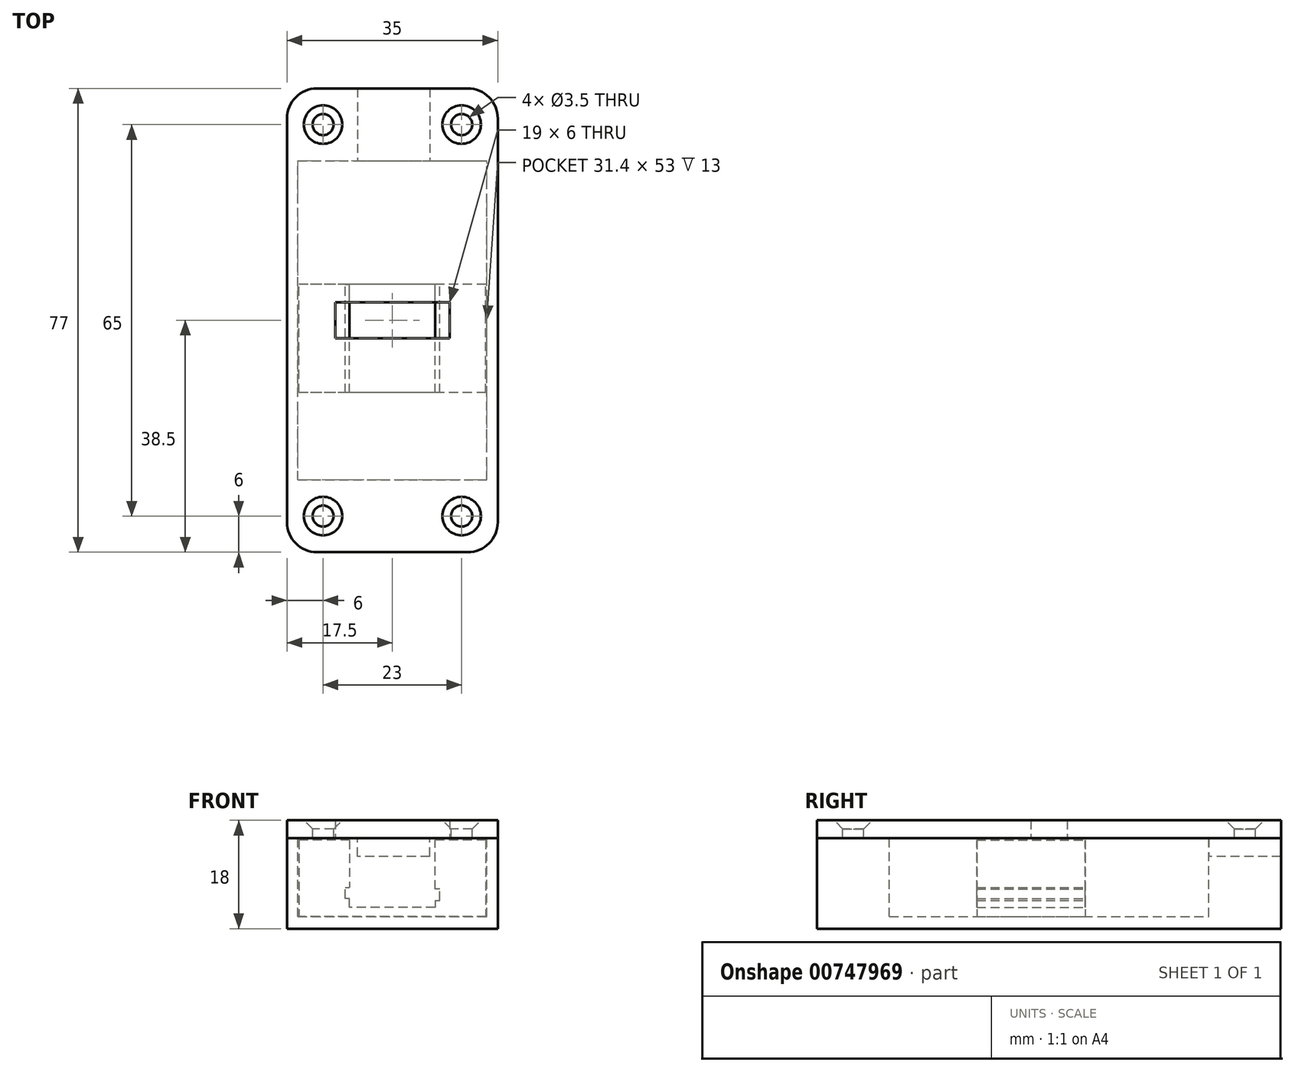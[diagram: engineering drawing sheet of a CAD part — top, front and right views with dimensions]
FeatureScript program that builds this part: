
annotation { "Feature Type Name" : "Feature", "Feature Type Description" : "" }
export const myFeature = defineFeature(function(context is Context, id is Id, definition is map)
    precondition{}
    {
        {
            var Q0;
            Q0=qCreatedBy(makeId("Top.planeOp"),FACE);
            var sketch = newSketch(context, id + "F0", { "sketchPlane" : qUnion([Q0])});
            skLineSegment(sketch, "E0.bottom", {"start": v(0, 0) * mm, "end": v(35, 0) * mm});
            skLineSegment(sketch, "E0.top", {"start": v(0, 77) * mm, "end": v(35, 77) * mm});
            skLineSegment(sketch, "E0.left", {"start": v(0, 0) * mm, "end": v(0, 77) * mm});
            skLineSegment(sketch, "E0.right", {"start": v(35, 0) * mm, "end": v(35, 77) * mm});
            skSolve(sketch);
        }
        {
            var Q0;
            Q0=makeQuery(id+"F0.imprint","IMPRINT",FACE,{"disambiguationData":[TD([[makeQuery(id+"F0.imprint","IMPRINT",EDGE,{"derivedFrom":sQuery(id+"F0.wireOp",EDGE,"E0.bottom")}),1.0]])]});
            extrude(context, id + "F1", {"entities" : qUnion([Q0]), "depth" : 15 * mm, "offsetDistance" : 25 * mm});
        }
        {
            var Q0;
            Q0=makeQuery(id+"F1.opExtrude","CAP_FACE",FACE,{"disambiguationData":[OSD([sQuery(id+"F0.wireOp",EDGE,"E0.bottom"),sQuery(id+"F0.wireOp",EDGE,"E0.top"),sQuery(id+"F0.wireOp",EDGE,"E0.left"),sQuery(id+"F0.wireOp",EDGE,"E0.right")])],"isStart":false});
            var sketch = newSketch(context, id + "F2", { "sketchPlane" : qUnion([Q0])});
            skLineSegment(sketch, "E1.bottom", {"start": v(1.8, 12) * mm, "end": v(33.2, 12) * mm});
            skLineSegment(sketch, "E1.top", {"start": v(1.8, 65) * mm, "end": v(33.2, 65) * mm});
            skLineSegment(sketch, "E1.left", {"start": v(1.8, 12) * mm, "end": v(1.8, 65) * mm});
            skLineSegment(sketch, "E1.right", {"start": v(33.2, 12) * mm, "end": v(33.2, 65) * mm});
            skSolve(sketch);
        }
        {
            var Q0;
            Q0=makeQuery(id+"F2.imprint","IMPRINT",FACE,{"disambiguationData":[TD([[makeQuery(id+"F2.imprint","IMPRINT",EDGE,{"derivedFrom":sQuery(id+"F2.wireOp",EDGE,"E1.bottom")}),1.0]])]});
            extrude(context, id + "F3", {"entities" : qUnion([Q0]), "operationType" : NewBodyOperationType.REMOVE, "oppositeDirection" : true, "depth" : 13 * mm, "offsetDistance" : 25 * mm});
        }
        {
            var Q0;
            Q0=makeQuery(id+"F3.boolean.opBoolean","COPY",FACE,{"derivedFrom":makeQuery(id+"F3.opExtrude","SWEPT_FACE",FACE,{"disambiguationData":[OSD([sQuery(id+"F2.wireOp",EDGE,"E1.top")])]})});
            var sketch = newSketch(context, id + "F4", { "sketchPlane" : qUnion([Q0])});
            skLineSegment(sketch, "E2.bottom", {"start": v(11.7, 15) * mm, "end": v(23.7, 15) * mm});
            skLineSegment(sketch, "E2.top", {"start": v(11.7, 12) * mm, "end": v(23.7, 12) * mm});
            skLineSegment(sketch, "E2.left", {"start": v(11.7, 15) * mm, "end": v(11.7, 12) * mm});
            skLineSegment(sketch, "E2.right", {"start": v(23.7, 15) * mm, "end": v(23.7, 12) * mm});
            skSolve(sketch);
        }
        {
            var Q0;
            Q0=makeQuery(id+"F4.imprint","IMPRINT",FACE,{"disambiguationData":[TD([[makeQuery(id+"F4.imprint","IMPRINT",EDGE,{"derivedFrom":sQuery(id+"F4.wireOp",EDGE,"E2.bottom")}),-1.0]])]});
            extrude(context, id + "F5", {"entities" : qUnion([Q0]), "operationType" : NewBodyOperationType.REMOVE, "oppositeDirection" : true, "depth" : 25 * mm, "offsetDistance" : 25 * mm});
        }
        {
            var Q0;
            Q0=makeQuery(id+"F1.opExtrude","CAP_FACE",FACE,{"disambiguationData":[OSD([sQuery(id+"F0.wireOp",EDGE,"E0.bottom"),sQuery(id+"F0.wireOp",EDGE,"E0.top"),sQuery(id+"F0.wireOp",EDGE,"E0.left"),sQuery(id+"F0.wireOp",EDGE,"E0.right")])],"isStart":false});
            var sketch = newSketch(context, id + "F6", { "sketchPlane" : qUnion([Q0])});
            skCircle(sketch, "E3", {"center": v(6, 6) * mm, "radius": 1.65 * mm});
            skCircle(sketch, "E4", {"center": v(29, 6) * mm, "radius": 1.65 * mm});
            skCircle(sketch, "E5", {"center": v(6, 71) * mm, "radius": 1.65 * mm});
            skCircle(sketch, "E6", {"center": v(29, 71) * mm, "radius": 1.65 * mm});
            skSolve(sketch);
        }
        {
            var Q0;
            Q0=makeQuery(id+"F6.imprint","IMPRINT",FACE,{"disambiguationData":[TD([[makeQuery(id+"F6.imprint","IMPRINT",EDGE,{"derivedFrom":sQuery(id+"F6.wireOp",EDGE,"E3")}),-1.0]])]});
            var sketch = newSketch(context, id + "F7", { "sketchPlane" : qUnion([Q0])});
            skLineSegment(sketch, "E7.bottom", {"start": v(0, 0) * mm, "end": v(35, 0) * mm});
            skLineSegment(sketch, "E7.top", {"start": v(0, 77) * mm, "end": v(35, 77) * mm});
            skLineSegment(sketch, "E7.left", {"start": v(0, 0) * mm, "end": v(0, 77) * mm});
            skLineSegment(sketch, "E7.right", {"start": v(35, 0) * mm, "end": v(35, 77) * mm});
            skSolve(sketch);
        }
        {
            var Q0;
            Q0 = qSketchRegion(id + "F7", true);
            extrude(context, id + "F8", {"entities" : qUnion([Q0]), "depth" : 3 * mm, "offsetDistance" : 25 * mm});
        }
        {
            var Q0;
            Q0=makeQuery(id+"F8.opExtrude","CAP_FACE",FACE,{"disambiguationData":[OSD([sQuery(id+"F7.wireOp",EDGE,"E7.bottom"),sQuery(id+"F7.wireOp",EDGE,"E7.top"),sQuery(id+"F7.wireOp",EDGE,"E7.left"),sQuery(id+"F7.wireOp",EDGE,"E7.right")])],"isStart":true});
            var sketch = newSketch(context, id + "F9", { "sketchPlane" : qUnion([Q0])});
            skLineSegment(sketch, "E8.bottom", {"start": v(8, -35.5) * mm, "end": v(27, -35.5) * mm});
            skLineSegment(sketch, "E8.top", {"start": v(8, -41.5) * mm, "end": v(27, -41.5) * mm});
            skLineSegment(sketch, "E8.left", {"start": v(8, -41.5) * mm, "end": v(8, -35.5) * mm});
            skLineSegment(sketch, "E8.right", {"start": v(27, -41.5) * mm, "end": v(27, -35.5) * mm});
            skPoint(sketch, "E9", {"position": v(27, -38.5) * mm});
            skSolve(sketch);
        }
        {
            var Q0;
            Q0=makeQuery(id+"F8.opExtrude","CAP_FACE",FACE,{"disambiguationData":[OSD([sQuery(id+"F7.wireOp",EDGE,"E7.bottom"),sQuery(id+"F7.wireOp",EDGE,"E7.top"),sQuery(id+"F7.wireOp",EDGE,"E7.left"),sQuery(id+"F7.wireOp",EDGE,"E7.right")])],"isStart":false});
            var sketch = newSketch(context, id + "F10", { "sketchPlane" : qUnion([Q0])});
            skPoint(sketch, "E10", {"position": v(29, 6) * mm});
            skPoint(sketch, "E11", {"position": v(6, 6) * mm});
            skPoint(sketch, "E12", {"position": v(6, 71) * mm});
            skPoint(sketch, "E13", {"position": v(29, 71) * mm});
            skSolve(sketch);
        }
        {
            var Q0;
            Q0=sQuery(id+"F10.wireOp",VERTEX,"E12");
            var Q1;
            Q1=sQuery(id+"F10.wireOp",VERTEX,"E13");
            var Q2;
            Q2=sQuery(id+"F10.wireOp",VERTEX,"E10");
            var Q3;
            Q3=sQuery(id+"F10.wireOp",VERTEX,"E11");
            var Q4;
            Q4=makeQuery(id+"F8.opExtrude","SWEPT_BODY",BODY,{"disambiguationData":[OSD([sQuery(id+"F7.wireOp",EDGE,"E7.bottom"),sQuery(id+"F7.wireOp",EDGE,"E7.top"),sQuery(id+"F7.wireOp",EDGE,"E7.left"),sQuery(id+"F7.wireOp",EDGE,"E7.right")])]});
            hole(context, id + "F11", {"style" : HoleStyle.C_SINK, "endStyle" : HoleEndStyle.THROUGH, "holeDiameter" : 3.5 * mm, "cSinkDiameter" : 6.4 * mm, "cSinkAngle" : 90 * degree, "majorDiameter" : 5 * mm, "isTappedThrough" : true, "tappedDepth" : 12 * mm, "tapClearance" : 3, "locations" : qUnion([Q0, Q1, Q2, Q3]), "scope" : qUnion([Q4])});
        }
        {
            var Q0;
            Q0=makeQuery(id+"F1.opExtrude","SWEPT_EDGE",EDGE,{"disambiguationData":[OSD([sQuery(id+"F0.wireOp",EDGE,"E0.top"),sQuery(id+"F0.wireOp",EDGE,"E0.right")])]});
            var Q1;
            Q1=makeQuery(id+"F8.opExtrude","SWEPT_EDGE",EDGE,{"disambiguationData":[OSD([sQuery(id+"F7.wireOp",EDGE,"E7.top"),sQuery(id+"F7.wireOp",EDGE,"E7.right")])]});
            var Q2;
            Q2=makeQuery(id+"F8.opExtrude","SWEPT_EDGE",EDGE,{"disambiguationData":[OSD([sQuery(id+"F7.wireOp",EDGE,"E7.top"),sQuery(id+"F7.wireOp",EDGE,"E7.left")])]});
            var Q3;
            Q3=makeQuery(id+"F1.opExtrude","SWEPT_EDGE",EDGE,{"disambiguationData":[OSD([sQuery(id+"F0.wireOp",EDGE,"E0.top"),sQuery(id+"F0.wireOp",EDGE,"E0.left")])]});
            var Q4;
            Q4=makeQuery(id+"F8.opExtrude","SWEPT_EDGE",EDGE,{"disambiguationData":[OSD([sQuery(id+"F7.wireOp",EDGE,"E7.bottom"),sQuery(id+"F7.wireOp",EDGE,"E7.right")])]});
            var Q5;
            Q5=makeQuery(id+"F1.opExtrude","SWEPT_EDGE",EDGE,{"disambiguationData":[OSD([sQuery(id+"F0.wireOp",EDGE,"E0.bottom"),sQuery(id+"F0.wireOp",EDGE,"E0.right")])]});
            var Q6;
            Q6=makeQuery(id+"F1.opExtrude","SWEPT_EDGE",EDGE,{"disambiguationData":[OSD([sQuery(id+"F0.wireOp",EDGE,"E0.bottom"),sQuery(id+"F0.wireOp",EDGE,"E0.left")])]});
            var Q7;
            Q7=makeQuery(id+"F8.opExtrude","SWEPT_EDGE",EDGE,{"disambiguationData":[OSD([sQuery(id+"F7.wireOp",EDGE,"E7.bottom"),sQuery(id+"F7.wireOp",EDGE,"E7.left")])]});
            fillet(context, id + "F12", {"entities" : qUnion([Q0, Q1, Q2, Q3, Q4, Q5, Q6, Q7]), "radius" : 5 * mm, "tangentPropagation" : true, "allowEdgeOverflow" : false});
        }
        {
            var Q0;
            Q0=makeQuery(id+"F3.boolean.opBoolean","COPY",FACE,{"derivedFrom":makeQuery(id+"F3.opExtrude","CAP_FACE",FACE,{"disambiguationData":[OSD([sQuery(id+"F2.wireOp",EDGE,"E1.bottom"),sQuery(id+"F2.wireOp",EDGE,"E1.top"),sQuery(id+"F2.wireOp",EDGE,"E1.left"),sQuery(id+"F2.wireOp",EDGE,"E1.right")])],"isStart":false})});
            var sketch = newSketch(context, id + "F13", { "sketchPlane" : qUnion([Q0])});
            skLineSegment(sketch, "E14.bottom", {"start": v(33, 26.5) * mm, "end": v(2, 26.5) * mm});
            skLineSegment(sketch, "E14.top", {"start": v(33, 44.5) * mm, "end": v(2, 44.5) * mm});
            skLineSegment(sketch, "E15", {"start": v(33, 26.5) * mm, "end": v(33, 44.5) * mm});
            skLineSegment(sketch, "E16", {"start": v(2, 26.5) * mm, "end": v(2, 44.5) * mm});
            skSolve(sketch);
        }
        {
            var Q0;
            Q0=makeQuery(id+"F13.imprint","IMPRINT",FACE,{"disambiguationData":[TD([[makeQuery(id+"F13.imprint","IMPRINT",EDGE,{"derivedFrom":sQuery(id+"F13.wireOp",EDGE,"E14.bottom")}),-1.0]])]});
            extrude(context, id + "F14", {"entities" : qUnion([Q0]), "endBound" : BoundingType.UP_TO_NEXT, "depth" : 8 * mm, "hasOffset" : true, "offsetDistance" : .3 * mm});
        }
        {
            var Q0;
            Q0=makeQuery(id+"F14.opExtrude","SWEPT_FACE",FACE,{"disambiguationData":[OSD([sQuery(id+"F13.wireOp",EDGE,"E14.top")])]});
            var sketch = newSketch(context, id + "F15", { "sketchPlane" : qUnion([Q0])});
            skLineSegment(sketch, "E17.left", {"start": v(-24.6, 10) * mm, "end": v(-24.6, 6.55) * mm});
            skLineSegment(sketch, "E17.right", {"start": v(-10.4, 10) * mm, "end": v(-10.4, 6.85) * mm});
            skLineSegment(sketch, "E18", {"start": v(-24.6, 4.7) * mm, "end": v(-25.35, 4.7) * mm});
            skLineSegment(sketch, "E19", {"start": v(-25.35, 4.7) * mm, "end": v(-25.35, 6.55) * mm});
            skLineSegment(sketch, "E20", {"start": v(-25.35, 6.55) * mm, "end": v(-24.6, 6.55) * mm});
            skLineSegment(sketch, "E21", {"start": v(-10.4, 5) * mm, "end": v(-9.65, 5) * mm});
            skLineSegment(sketch, "E22", {"start": v(-9.65, 5) * mm, "end": v(-9.65, 6.85) * mm});
            skLineSegment(sketch, "E23", {"start": v(-9.65, 6.85) * mm, "end": v(-10.4, 6.85) * mm});
            skLineSegment(sketch, "E24", {"start": v(-24.6, 4.7) * mm, "end": v(-24.6, 3.5) * mm});
            skLineSegment(sketch, "E25", {"start": v(-24.6, 3.5) * mm, "end": v(-10.4, 3.5) * mm});
            skLineSegment(sketch, "E26", {"start": v(-10.4, 3.5) * mm, "end": v(-10.4, 5) * mm});
            skLineSegment(sketch, "E27", {"start": v(-24.6, 10) * mm, "end": v(-24.6, 14.7) * mm});
            skLineSegment(sketch, "E28", {"start": v(-10.4, 10) * mm, "end": v(-10.4, 14.7) * mm});
            skLineSegment(sketch, "E29", {"start": v(-10.4, 14.7) * mm, "end": v(-24.6, 14.7) * mm});
            skSolve(sketch);
        }
        {
            var Q0;
            Q0=makeQuery(id+"F15.imprint","IMPRINT",FACE,{"disambiguationData":[TD([[makeQuery(id+"F15.imprint","IMPRINT",EDGE,{"derivedFrom":sQuery(id+"F15.wireOp",EDGE,"E17.bottom")}),-1.0]])]});
            var Q1;
            Q1=makeQuery(id+"F15.imprint","IMPRINT",FACE,{"disambiguationData":[TD([[makeQuery(id+"F15.imprint","IMPRINT",EDGE,{"derivedFrom":sQuery(id+"F15.wireOp",EDGE,"E17.left")}),1.0]])]});
            extrude(context, id + "F16", {"entities" : qUnion([Q0, Q1]), "operationType" : NewBodyOperationType.REMOVE, "endBound" : BoundingType.UP_TO_NEXT, "oppositeDirection" : true, "depth" : 25 * mm, "offsetDistance" : 25 * mm});
        }
        {
            var Q0;
            Q0=makeQuery(id+"F9.imprint","IMPRINT",FACE,{"disambiguationData":[TD([[makeQuery(id+"F9.imprint","IMPRINT",EDGE,{"derivedFrom":sQuery(id+"F9.wireOp",EDGE,"E8.bottom")}),-1.0]])]});
            extrude(context, id + "F17", {"entities" : qUnion([Q0]), "operationType" : NewBodyOperationType.REMOVE, "endBound" : BoundingType.UP_TO_NEXT, "oppositeDirection" : true, "depth" : 25 * mm, "offsetDistance" : 25 * mm});
        }
    });
